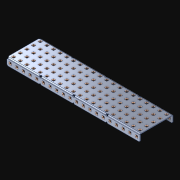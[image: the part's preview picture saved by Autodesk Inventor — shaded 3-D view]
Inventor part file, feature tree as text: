
AUTODESK INVENTOR PART (.ipt)
format: ipt  version: 2021 (Build 250183000, 183)  size: 1,972,224 bytes
history: native  units: in
note: dims shown in document units (in); Inventor stores cm internally (conversion verified against a paired STEP export)
features: extrude x141, other x141, sketch x4, pattern_linear x3
ambient origin geometry x8: Origin, YZ Plane, XZ Plane, XY Plane, X Axis, Y Axis, Z Axis, Center Point
bodies: Solid1 (feature_tree)
feature tree (289):
  pattern_linear  "Rectangular Pattern1"  Spacing1=0.182in  [1 undecoded]
  pattern_linear  "Rectangular Pattern2"  Spacing1=0.046in  [1 undecoded]
  pattern_linear  "Rectangular Pattern3"  Spacing1=0.5in  [1 undecoded]
  extrude  "Extrusion1"  Depth=0.046in
  sketch  "Sketch1"  dims[d0=0.182in]
  other  "Srf1"
  sketch  "Sketch2"  dims[d1=0.046in d2=0.0in]
  other  "Srf2"
  sketch  "Sketch3"  dims[d3=0.182in]
  other  "Srf3"
  other  "Srf4"
  other  "Srf5"
  other  "Srf6"
  other  "Srf7"
  other  "Srf8"
  other  "Srf9"
  other  "Srf10"
  other  "Srf11"
  other  "Srf12"
  other  "Srf13"
  other  "Srf14"
  other  "Srf15"
  other  "Srf16"
  other  "Srf17"
  other  "Srf18"
  other  "Srf19"
  other  "Srf20"
  other  "Srf21"
  other  "Srf22"
  other  "Srf38"
  other  "Srf39"
  other  "Srf40"
  other  "Srf41"
  other  "Srf42"
  other  "Srf43"
  other  "Srf44"
  other  "Srf45"
  other  "Srf46"
  other  "Srf47"
  other  "Srf48"
  other  "Srf49"
  other  "Srf50"
  other  "Srf51"
  other  "Srf52"
  other  "Srf53"
  other  "Srf54"
  other  "Srf55"
  other  "Srf56"
  other  "Srf72"
  other  "Srf73"
  other  "Srf74"
  other  "Srf75"
  other  "Srf76"
  other  "Srf77"
  other  "Srf78"
  other  "Srf79"
  other  "Srf80"
  other  "Srf81"
  other  "Srf82"
  other  "Srf83"
  other  "Srf84"
  other  "Srf85"
  other  "Srf86"
  other  "Srf87"
  other  "Srf88"
  other  "Srf89"
  other  "Srf90"
  other  "Srf91"
  other  "Srf107"
  other  "Srf108"
  other  "Srf109"
  other  "Srf110"
  other  "Srf111"
  other  "Srf112"
  other  "Srf113"
  other  "Srf114"
  other  "Srf115"
  other  "Srf116"
  other  "Srf117"
  other  "Srf118"
  other  "Srf119"
  other  "Srf120"
  other  "Srf121"
  other  "Srf122"
  other  "Srf123"
  other  "Srf124"
  other  "Srf125"
  other  "Srf126"
  other  "Srf142"
  other  "Srf143"
  other  "Srf144"
  other  "Srf145"
  other  "Srf146"
  other  "Srf147"
  other  "Srf148"
  other  "Srf149"
  other  "Srf150"
  other  "Srf151"
  other  "Srf152"
  other  "Srf153"
  other  "Srf154"
  other  "Srf155"
  other  "Srf156"
  other  "Srf157"
  other  "Srf158"
  other  "Srf159"
  other  "Srf160"
  other  "Srf161"
  other  "Srf177"
  other  "Srf178"
  other  "Srf179"
  other  "Srf180"
  other  "Srf181"
  other  "Srf182"
  other  "Srf183"
  other  "Srf184"
  other  "Srf185"
  other  "Srf186"
  other  "Srf187"
  other  "Srf188"
  other  "Srf189"
  other  "Srf190"
  other  "Srf191"
  other  "Srf192"
  other  "Srf193"
  other  "Srf194"
  other  "Srf195"
  other  "Srf196"
  other  "Srf212"
  other  "Srf213"
  other  "Srf214"
  other  "Srf215"
  other  "Srf216"
  other  "Srf217"
  other  "Srf218"
  other  "Srf219"
  other  "Srf220"
  other  "Srf221"
  other  "Srf222"
  other  "Srf223"
  other  "Srf224"
  other  "Srf225"
  other  "Srf226"
  other  "Srf227"
  other  "Srf228"
  other  "Srf229"
  other  "Srf230"
  sketch  "Sketch4"  dims[d4=0.046in d5=0.0in d6=0.182in d7=0.046in d8=0.0in d11=0.5in d12=7.874in d14=0.5in d15=1.9685in d17=0.5in d18=7.874in d20=0.5in d21=7.5in d22=0.0in]
  parser-record x1  (decoder bookkeeping rows leaked as tree rows — omitted from the tree; the rows remain in map.json)
  extrude  "ExtrusionSrf1"  Depth=0.046in
  extrude  "ExtrusionSrf2"  Depth=0.046in
  extrude  "ExtrusionSrf3"  Depth=0.046in
  extrude  "ExtrusionSrf4"  Depth=0.046in
  extrude  "ExtrusionSrf5"  Depth=0.046in
  extrude  "ExtrusionSrf6"  TaperAngle=0.0deg  [1 undecoded]
  extrude  "ExtrusionSrf7"  [1 undecoded]
  extrude  "ExtrusionSrf8"  [1 undecoded]
  extrude  "ExtrusionSrf9"  [1 undecoded]
  extrude  "ExtrusionSrf10"  [1 undecoded]
  extrude  "ExtrusionSrf11"  [1 undecoded]
  extrude  "ExtrusionSrf12"  [1 undecoded]
  extrude  "ExtrusionSrf13"  [1 undecoded]
  extrude  "ExtrusionSrf14"  [1 undecoded]
  extrude  "ExtrusionSrf15"  [1 undecoded]
  extrude  "ExtrusionSrf16"  [1 undecoded]
  extrude  "ExtrusionSrf17"  [1 undecoded]
  extrude  "ExtrusionSrf18"  [1 undecoded]
  extrude  "ExtrusionSrf19"  [1 undecoded]
  extrude  "ExtrusionSrf20"  [1 undecoded]
  extrude  "ExtrusionSrf21"  [1 undecoded]
  extrude  "ExtrusionSrf22"  [1 undecoded]
  extrude  "ExtrusionSrf38"  [1 undecoded]
  extrude  "ExtrusionSrf39"  [1 undecoded]
  extrude  "ExtrusionSrf40"  [1 undecoded]
  extrude  "ExtrusionSrf41"  [1 undecoded]
  extrude  "ExtrusionSrf42"  [1 undecoded]
  extrude  "ExtrusionSrf43"  [1 undecoded]
  extrude  "ExtrusionSrf44"  [1 undecoded]
  extrude  "ExtrusionSrf45"  [1 undecoded]
  extrude  "ExtrusionSrf46"  [1 undecoded]
  extrude  "ExtrusionSrf47"  [1 undecoded]
  extrude  "ExtrusionSrf48"  [1 undecoded]
  extrude  "ExtrusionSrf49"  [1 undecoded]
  extrude  "ExtrusionSrf50"  [1 undecoded]
  extrude  "ExtrusionSrf51"  [1 undecoded]
  extrude  "ExtrusionSrf52"  [1 undecoded]
  extrude  "ExtrusionSrf53"  [1 undecoded]
  extrude  "ExtrusionSrf54"  [1 undecoded]
  extrude  "ExtrusionSrf55"  [1 undecoded]
  extrude  "ExtrusionSrf56"  [1 undecoded]
  extrude  "ExtrusionSrf72"  [1 undecoded]
  extrude  "ExtrusionSrf73"  [1 undecoded]
  extrude  "ExtrusionSrf74"  [1 undecoded]
  extrude  "ExtrusionSrf75"  [1 undecoded]
  extrude  "ExtrusionSrf76"  [1 undecoded]
  extrude  "ExtrusionSrf77"  [1 undecoded]
  extrude  "ExtrusionSrf78"  [1 undecoded]
  extrude  "ExtrusionSrf79"  [1 undecoded]
  extrude  "ExtrusionSrf80"  [1 undecoded]
  extrude  "ExtrusionSrf81"  [1 undecoded]
  extrude  "ExtrusionSrf82"  [1 undecoded]
  extrude  "ExtrusionSrf83"  [1 undecoded]
  extrude  "ExtrusionSrf84"  [1 undecoded]
  extrude  "ExtrusionSrf85"  [1 undecoded]
  extrude  "ExtrusionSrf86"  [1 undecoded]
  extrude  "ExtrusionSrf87"  [1 undecoded]
  extrude  "ExtrusionSrf88"  [1 undecoded]
  extrude  "ExtrusionSrf89"  [1 undecoded]
  extrude  "ExtrusionSrf90"  [1 undecoded]
  extrude  "ExtrusionSrf91"  [1 undecoded]
  extrude  "ExtrusionSrf107"  [1 undecoded]
  extrude  "ExtrusionSrf108"  [1 undecoded]
  extrude  "ExtrusionSrf109"  [1 undecoded]
  extrude  "ExtrusionSrf110"  [1 undecoded]
  extrude  "ExtrusionSrf111"  [1 undecoded]
  extrude  "ExtrusionSrf112"  [1 undecoded]
  extrude  "ExtrusionSrf113"  [1 undecoded]
  extrude  "ExtrusionSrf114"  [1 undecoded]
  extrude  "ExtrusionSrf115"  [1 undecoded]
  extrude  "ExtrusionSrf116"  [1 undecoded]
  extrude  "ExtrusionSrf117"  [1 undecoded]
  extrude  "ExtrusionSrf118"  [1 undecoded]
  extrude  "ExtrusionSrf119"  [1 undecoded]
  extrude  "ExtrusionSrf120"  [1 undecoded]
  extrude  "ExtrusionSrf121"  [1 undecoded]
  extrude  "ExtrusionSrf122"  [1 undecoded]
  extrude  "ExtrusionSrf123"  [1 undecoded]
  extrude  "ExtrusionSrf124"  [1 undecoded]
  extrude  "ExtrusionSrf125"  [1 undecoded]
  extrude  "ExtrusionSrf126"  [1 undecoded]
  extrude  "ExtrusionSrf142"  [1 undecoded]
  extrude  "ExtrusionSrf143"  [1 undecoded]
  extrude  "ExtrusionSrf144"  [1 undecoded]
  extrude  "ExtrusionSrf145"  [1 undecoded]
  extrude  "ExtrusionSrf146"  [1 undecoded]
  extrude  "ExtrusionSrf147"  [1 undecoded]
  extrude  "ExtrusionSrf148"  [1 undecoded]
  extrude  "ExtrusionSrf149"  [1 undecoded]
  extrude  "ExtrusionSrf150"  [1 undecoded]
  extrude  "ExtrusionSrf151"  [1 undecoded]
  extrude  "ExtrusionSrf152"  [1 undecoded]
  extrude  "ExtrusionSrf153"  [1 undecoded]
  extrude  "ExtrusionSrf154"  [1 undecoded]
  extrude  "ExtrusionSrf155"  [1 undecoded]
  extrude  "ExtrusionSrf156"  [1 undecoded]
  extrude  "ExtrusionSrf157"  [1 undecoded]
  extrude  "ExtrusionSrf158"  [1 undecoded]
  extrude  "ExtrusionSrf159"  [1 undecoded]
  extrude  "ExtrusionSrf160"  [1 undecoded]
  extrude  "ExtrusionSrf161"  [1 undecoded]
  extrude  "ExtrusionSrf177"  [1 undecoded]
  extrude  "ExtrusionSrf178"  [1 undecoded]
  extrude  "ExtrusionSrf179"  [1 undecoded]
  extrude  "ExtrusionSrf180"  [1 undecoded]
  extrude  "ExtrusionSrf181"  [1 undecoded]
  extrude  "ExtrusionSrf182"  [1 undecoded]
  extrude  "ExtrusionSrf183"  [1 undecoded]
  extrude  "ExtrusionSrf184"  [1 undecoded]
  extrude  "ExtrusionSrf185"  [1 undecoded]
  extrude  "ExtrusionSrf186"  [1 undecoded]
  extrude  "ExtrusionSrf187"  [1 undecoded]
  extrude  "ExtrusionSrf188"  [1 undecoded]
  extrude  "ExtrusionSrf189"  [1 undecoded]
  extrude  "ExtrusionSrf190"  [1 undecoded]
  extrude  "ExtrusionSrf191"  [1 undecoded]
  extrude  "ExtrusionSrf192"  [1 undecoded]
  extrude  "ExtrusionSrf193"  [1 undecoded]
  extrude  "ExtrusionSrf194"  [1 undecoded]
  extrude  "ExtrusionSrf195"  [1 undecoded]
  extrude  "ExtrusionSrf196"  [1 undecoded]
  extrude  "ExtrusionSrf212"  [1 undecoded]
  extrude  "ExtrusionSrf213"  [1 undecoded]
  extrude  "ExtrusionSrf214"  [1 undecoded]
  extrude  "ExtrusionSrf215"  [1 undecoded]
  extrude  "ExtrusionSrf216"  [1 undecoded]
  extrude  "ExtrusionSrf217"  [1 undecoded]
  extrude  "ExtrusionSrf218"  [1 undecoded]
  extrude  "ExtrusionSrf219"  [1 undecoded]
  extrude  "ExtrusionSrf220"  [1 undecoded]
  extrude  "ExtrusionSrf221"  [1 undecoded]
  extrude  "ExtrusionSrf222"  [1 undecoded]
  extrude  "ExtrusionSrf223"  [1 undecoded]
  extrude  "ExtrusionSrf224"  [1 undecoded]
  extrude  "ExtrusionSrf225"  [1 undecoded]
  extrude  "ExtrusionSrf226"  [1 undecoded]
  extrude  "ExtrusionSrf227"  [1 undecoded]
  extrude  "ExtrusionSrf228"  [1 undecoded]
  extrude  "ExtrusionSrf229"  [1 undecoded]
  extrude  "ExtrusionSrf230"  [1 undecoded]
note: 138 required parameter values undecoded (feature->parameter linkage not recoverable at this tier; creation-order binding heuristic only, values carry confidence <= 0.55)
